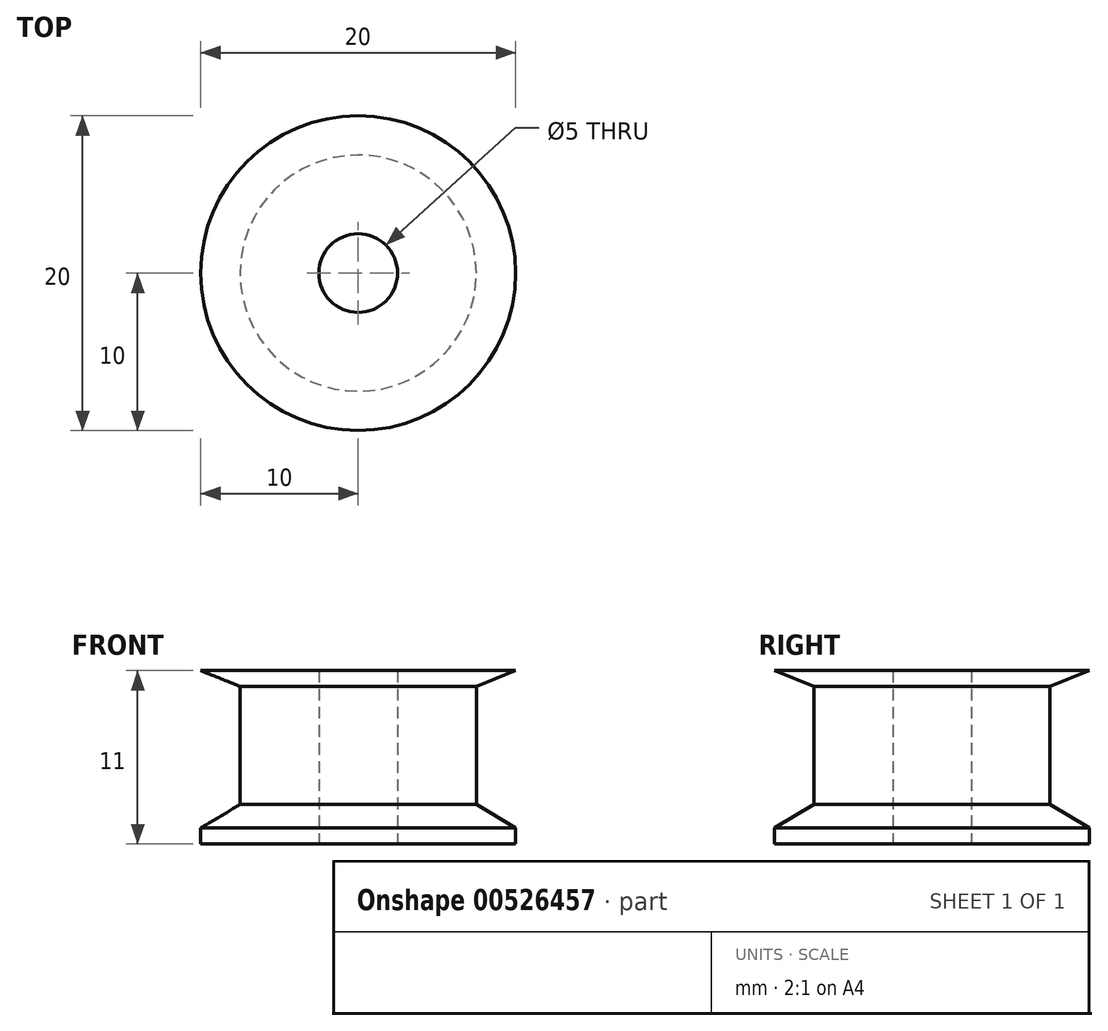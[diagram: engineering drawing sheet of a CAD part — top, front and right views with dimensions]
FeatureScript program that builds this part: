
annotation { "Feature Type Name" : "Feature", "Feature Type Description" : "" }
export const myFeature = defineFeature(function(context is Context, id is Id, definition is map)
    precondition{}
    {
        {
            var Q0;
            Q0=qCreatedBy(makeId("Front.planeOp"),FACE);
            var sketch = newSketch(context, id + "F0", { "sketchPlane" : qUnion([Q0])});
            skLineSegment(sketch, "E0", {"start": v(2.5, 11) * mm, "end": v(10, 11) * mm});
            skLineSegment(sketch, "E1", {"start": v(10, 11) * mm, "end": v(7.5, 10) * mm});
            skLineSegment(sketch, "E2", {"start": v(7.5, 10) * mm, "end": v(7.5, 2.5) * mm});
            skLineSegment(sketch, "E3", {"start": v(7.5, 2.5) * mm, "end": v(10, 1) * mm});
            skLineSegment(sketch, "E4", {"start": v(10, 1) * mm, "end": v(10, 0) * mm});
            skLineSegment(sketch, "E5", {"start": v(10, 0) * mm, "end": v(2.5, 0) * mm});
            skLineSegment(sketch, "E6", {"start": v(2.5, 0) * mm, "end": v(2.5, 11) * mm});
            skLineSegment(sketch, "E7", {"start": v(0, 0) * mm, "end": v(0, 14.55) * mm, "construction": true});
            skSolve(sketch);
        }
        {
            var Q0;
            Q0 = qSketchRegion(id + "F0", true);
            var Q1;
            Q1=sQuery(id+"F0.wireOp",EDGE,"E7");
            revolve(context, id + "F1", {"surfaceOperationType" : NewSurfaceOperationType.NEW, "entities" : qUnion([Q0]), "axis" : qUnion([Q1]), "revolveType" : RevolveType.FULL});
        }
    });
